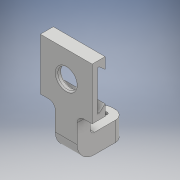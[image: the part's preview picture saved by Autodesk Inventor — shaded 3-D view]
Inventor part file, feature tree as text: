
AUTODESK INVENTOR PART (.ipt)
format: ipt  version: 2017 (Build 210142000, 142)  size: 197,120 bytes
history: native  units: mm
features: extrude x5, fillet x5, sketch x4, hole x1
ambient origin geometry x8: Origin, YZ Plane, XZ Plane, XY Plane, X Axis, Y Axis, Z Axis, Center Point
bodies: Solid1 (feature_tree)
feature tree (15):
  extrude  "Block"  Depth=15.0mm
  extrude  "Tripod Slot"  Depth=60.0mm
  hole  "Hole1"  [1 undecoded]
  extrude  "Extrusion4"  Depth=17.3mm
  extrude  "Extrusion5"  Depth=17.3mm
  extrude  "Extrusion6"  Depth=17.3mm
  fillet  "Fillet4"  Radius=60.0mm
  fillet  "Fillet5"  Radius=30.0mm
  fillet  "Fillet6"  Radius=49.5mm
  fillet  "Fillet10"  Radius=40.0mm
  fillet  "Fillet11"  Radius=5.0mm
  sketch  "Sketch2"  dims[d0=60.0mm d1=15.0mm]
  sketch  "Sketch4"  dims[d14=60.0mm d15=0.0mm d17=17.25mm]
  sketch  "Sketch5"  dims[d18=17.25mm d19=8.9mm]
  sketch  "Sketch6"  dims[d20=23.25mm d21=23.25mm d22=2.0mm d23=2.0mm d24=60.0mm d25=0.0mm d46=30.0mm d47=30.0mm d48=22.5mm d49=6.0mm d50=4.0mm d51=2.0mm d52=90.0deg d53=8.0mm d54=20.594885mm d55=49.5mm d56=0.0mm d58=40.0mm d59=0.0mm d60=5.0mm d61=10.0mm d62=31.75mm d63=0.0mm d64=25.4mm d67=22.5mm d68=3.0mm d70=11.0mm d71=20.0mm d72=5.0mm d94=7.5mm d95=1.5mm d96=17.3mm d97=9.0mm d98=12.7mm d99=22.957255mm]
note: 1 required parameter value undecoded (feature->parameter linkage not recoverable at this tier; creation-order binding heuristic only, values carry confidence <= 0.55)
